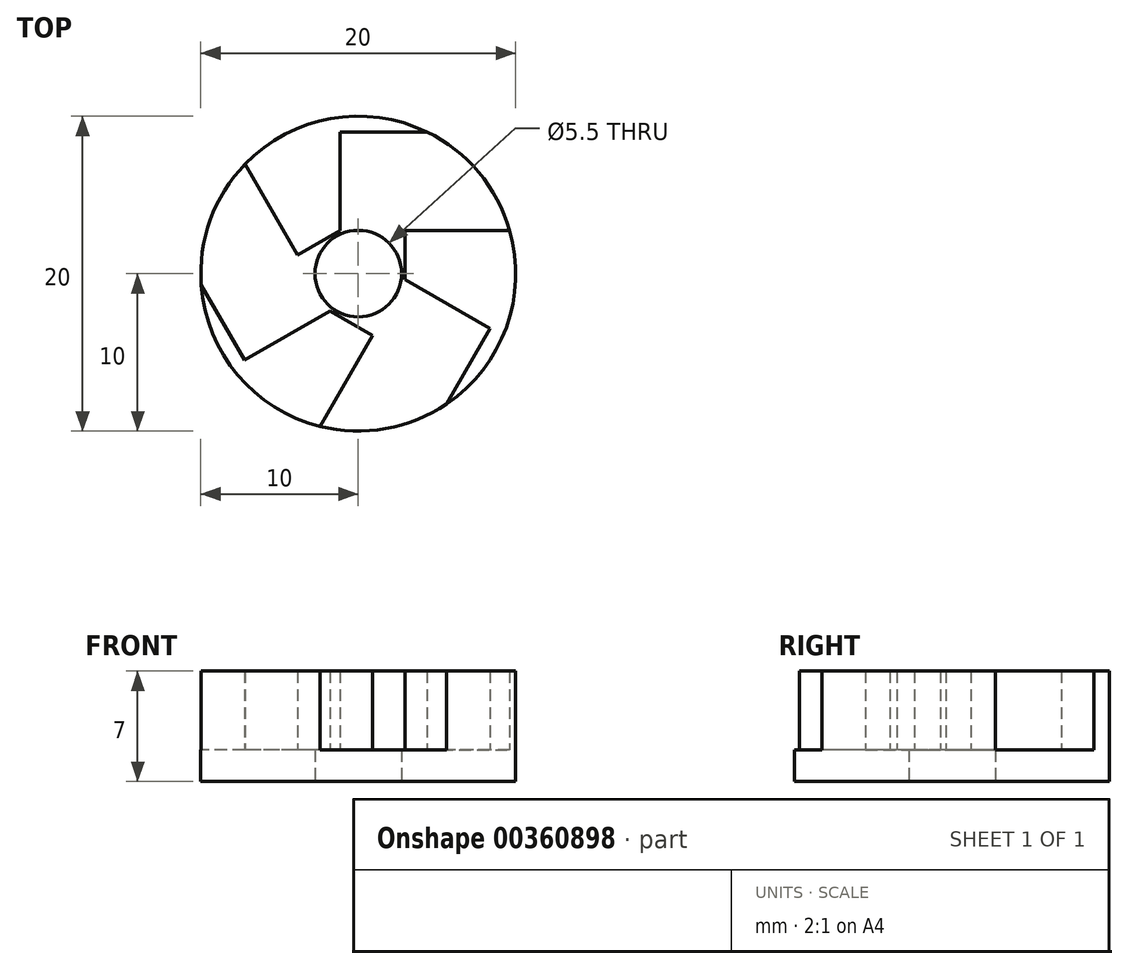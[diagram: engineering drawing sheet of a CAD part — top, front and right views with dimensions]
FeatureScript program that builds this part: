
annotation { "Feature Type Name" : "Feature", "Feature Type Description" : "" }
export const myFeature = defineFeature(function(context is Context, id is Id, definition is map)
    precondition{}
    {
        {
            var Q0;
            Q0=qCreatedBy(makeId("Top.planeOp"),FACE);
            var sketch = newSketch(context, id + "F0", { "sketchPlane" : qUnion([Q0])});
            skCircle(sketch, "E0", {"center": v(0, 0) * mm, "radius": 10 * mm});
            skCircle(sketch, "E1", {"center": v(0, 0) * mm, "radius": 2.75 * mm});
            skLineSegment(sketch, "E2", {"start": v(-1.15, 2.75) * mm, "end": v(9.61, 2.75) * mm});
            skLineSegment(sketch, "E3.0", {"start": v(-1.15, 9) * mm, "end": v(4.36, 9) * mm});
            skLineSegment(sketch, "E4.1.0", {"start": v(-7.22, -5.5) * mm, "end": v(-9.97, -0.73) * mm});
            skLineSegment(sketch, "E4.1.1", {"start": v(-1.8, -2.37) * mm, "end": v(-7.19, 6.95) * mm});
            skLineSegment(sketch, "E4.2.0", {"start": v(8.37, -3.5) * mm, "end": v(5.61, -8.27) * mm});
            skLineSegment(sketch, "E4.2.1", {"start": v(2.96, -0.38) * mm, "end": v(-2.43, -9.7) * mm});
            skLineSegment(sketch, "E5", {"start": v(2.96, -0.38) * mm, "end": v(8.37, -3.5) * mm});
            skPoint(sketch, "E6.orphan", {"position": v(7.8, -4.5) * mm});
            skPoint(sketch, "E7.orphan", {"position": v(2.38, -1.38) * mm});
            skLineSegment(sketch, "E8.1.0", {"start": v(-1.15, 2.75) * mm, "end": v(-1.15, 9) * mm});
            skLineSegment(sketch, "E8.2.0", {"start": v(-1.8, -2.37) * mm, "end": v(-7.22, -5.5) * mm});
            skPoint(sketch, "E9.orphan", {"position": v(0, 9) * mm});
            skPoint(sketch, "E10.orphan", {"position": v(0, 2.75) * mm});
            skPoint(sketch, "E11.orphan", {"position": v(-2.38, -1.38) * mm});
            skPoint(sketch, "E12.orphan", {"position": v(-7.8, -4.5) * mm});
            skLineSegment(sketch, "E13", {"start": v(2.96, -0.38) * mm, "end": v(2.96, 2.75) * mm});
            skLineSegment(sketch, "E14.1.0", {"start": v(-1.15, 2.75) * mm, "end": v(-3.86, 1.19) * mm});
            skLineSegment(sketch, "E14.2.0", {"start": v(-1.8, -2.37) * mm, "end": v(0.9, -3.94) * mm});
            skPoint(sketch, "E15.orphan", {"position": v(2.74, -0.25) * mm});
            skPoint(sketch, "E16.orphan", {"position": v(-1.59, -2.25) * mm});
            skPoint(sketch, "E17.orphan", {"position": v(-1.15, 2.5) * mm});
            skSolve(sketch);
        }
        {
            var Q0;
            {var subQ0=sQuery(id+"F0.wireOp",EDGE,"E3.0");Q0=makeQuery(id+"F0.imprint","IMPRINT",FACE,{"disambiguationData":[TD([[makeQuery(id+"F0.imprint","IMPRINT",EDGE,{"derivedFrom":subQ0}),-1.0]])]});}
            var Q1;
            {var subQ4=sQuery(id+"F0.wireOp",EDGE,"E4.1.0");Q1=makeQuery(id+"F0.imprint","IMPRINT",FACE,{"disambiguationData":[TD([[makeQuery(id+"F0.imprint","IMPRINT",EDGE,{"derivedFrom":subQ4}),-1.0]])]});}
            var Q2;
            {var subQ4=sQuery(id+"F0.wireOp",EDGE,"E4.2.0");Q2=makeQuery(id+"F0.imprint","IMPRINT",FACE,{"disambiguationData":[TD([[makeQuery(id+"F0.imprint","IMPRINT",EDGE,{"derivedFrom":subQ4}),-1.0]])]});}
            var Q3;
            {var subQ0=sQuery(id+"F0.wireOp",EDGE,"E8.2.0");var subQ1=sQuery(id+"F0.wireOp",EDGE,"E1");var subQ2=makeQuery(id+"F0.imprint","INTERSECT",VERTEX,{"derivedFrom":[subQ1,subQ0]});Q3=makeQuery(id+"F0.imprint","IMPRINT",FACE,{"disambiguationData":[TD([[makeQuery(id+"F0.imprint","IMPRINT",EDGE,{"disambiguationData":[TD([[subQ2,1.0]])],"derivedFrom":subQ1}),-1.0]])]});}
            var Q4;
            {var subQ0=sQuery(id+"F0.wireOp",EDGE,"E5");var subQ1=sQuery(id+"F0.wireOp",EDGE,"E1");var subQ2=makeQuery(id+"F0.imprint","INTERSECT",VERTEX,{"derivedFrom":[subQ1,subQ0]});Q4=makeQuery(id+"F0.imprint","IMPRINT",FACE,{"disambiguationData":[TD([[makeQuery(id+"F0.imprint","IMPRINT",EDGE,{"disambiguationData":[TD([[subQ2,1.0]])],"derivedFrom":subQ1}),-1.0]])]});}
            var Q5;
            {var subQ0=sQuery(id+"F0.wireOp",EDGE,"E8.1.0");var subQ1=sQuery(id+"F0.wireOp",EDGE,"E1");var subQ2=makeQuery(id+"F0.imprint","INTERSECT",VERTEX,{"derivedFrom":[subQ1,subQ0]});Q5=makeQuery(id+"F0.imprint","IMPRINT",FACE,{"disambiguationData":[TD([[makeQuery(id+"F0.imprint","IMPRINT",EDGE,{"disambiguationData":[TD([[subQ2,1.0]])],"derivedFrom":subQ1}),-1.0]])]});}
            extrude(context, id + "F1", {"entities" : qUnion([Q0, Q1, Q2, Q3, Q4, Q5]), "depth" : 2 * mm, "offsetDistance" : 25 * mm});
        }
        {
            var Q0;
            {var subQ0=sQuery(id+"F0.wireOp",EDGE,"E3.0");Q0=makeQuery(id+"F0.imprint","IMPRINT",FACE,{"disambiguationData":[TD([[makeQuery(id+"F0.imprint","IMPRINT",EDGE,{"derivedFrom":subQ0}),1.0]])]});}
            var Q1;
            {var subQ0=sQuery(id+"F0.wireOp",EDGE,"E4.2.0");Q1=makeQuery(id+"F0.imprint","IMPRINT",FACE,{"disambiguationData":[TD([[makeQuery(id+"F0.imprint","IMPRINT",EDGE,{"derivedFrom":subQ0}),1.0]])]});}
            var Q2;
            {var subQ4=sQuery(id+"F0.wireOp",EDGE,"E4.1.0");Q2=makeQuery(id+"F0.imprint","IMPRINT",FACE,{"disambiguationData":[TD([[makeQuery(id+"F0.imprint","IMPRINT",EDGE,{"derivedFrom":subQ4}),1.0]])]});}
            extrude(context, id + "F2", {"entities" : qUnion([Q0, Q1, Q2]), "operationType" : NewBodyOperationType.ADD, "depth" : 7 * mm, "offsetDistance" : 25 * mm});
        }
    });
